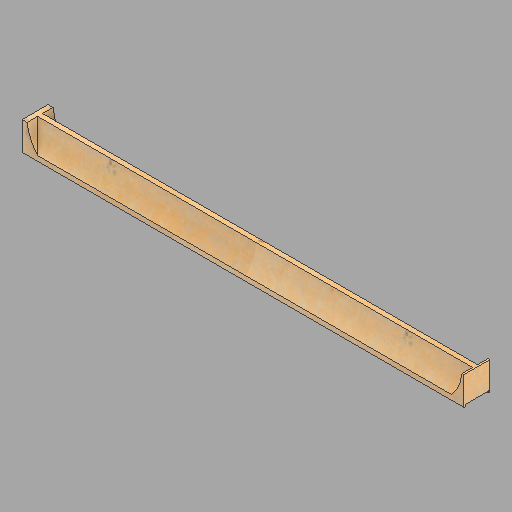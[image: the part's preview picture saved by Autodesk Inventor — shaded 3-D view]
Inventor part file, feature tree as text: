
AUTODESK INVENTOR PART (.ipt)
format: ipt  version: 2022.2 (Build 262287010, 287A)  size: 180,736 bytes
history: native  units: in
note: dims shown in document units (in); Inventor stores cm internally (conversion verified against a paired STEP export)
features: direct_edit x1, other x1, revolve x1
ambient origin geometry x8: Origin, YZ Plane, XZ Plane, XY Plane, X Axis, Y Axis, Z Axis, Center Point
bodies: Solid1 (feature_tree)
feature tree (3):
  direct_edit  "Direct Edit1"
  other  "Upper Jamb (2) (1)"
  revolve  "Rotate1"  [1 undecoded]
note: 1 required parameter value undecoded (feature->parameter linkage not recoverable at this tier; creation-order binding heuristic only, values carry confidence <= 0.55)
